# Revit family: result
name_source: partatom
category: Plumbing Fixtures
revit_build: Autodesk Revit 2015 (Build: 20140903_1530(x64)
units: mm (PartAtom-declared; Revit-internal decimal feet)

## types (1)
- Default
    BIMobject category = Toilet Cisterns
    BIMobject category code = sanitary-toilet-cisterns
    BIMobject main category = Sanitary
    BIMobject main category code = sanitary
    Brand url = http://www.duravit.com
    Edition number = 1
    GTIN code = https://4063382015969
    IFC Classification = Sanitary Terminal
    Manufacturer name = DURAVIT
    Masterformat 2014 Code = 01 52 19
    Masterformat 2014 Description = Sanitary Facilities
    Material main = Ceramics
    NBS Reference Code = 35-93-90
    NBS Reference Description = Wc Cisterns
    OmniClass Code = 23-31 19 00
    OmniClass Description = Toilets
    Product Guid = 4cff327e-d83d-4afb-8281-cba8cef9f96d
    Product SKU = d-neo-tank-094400
    Product data url = https://bimobject.com
    Product family = D-Neo
    Product group = Tank
    Product name = 094400 D-Neo Tank
    Product url = https://duravit-public-assets.s3.eu-central-1.amazonaws.com
    QR code = http://bimobject.com
    UNSPSC Code = 30181515
    Uniclass 1.4 Code = L72164
    Uniclass 1.4 Description = WC cisterns
    Uniclass 2.0 Code = PR-35-93-90
    Uniclass 2.0 Description = Wc Cisterns
    Uniclass 2015 Code = Pr_40_20_93_89
    Uniclass 2015 Name = WC cisterns
    Uniformat II Code = D2010
    Uniformat II Description = Plumbing Fixtures

## geometry (parser evidence)
native form markers: Sweep x4
no freeform markers — native parametric forms only
